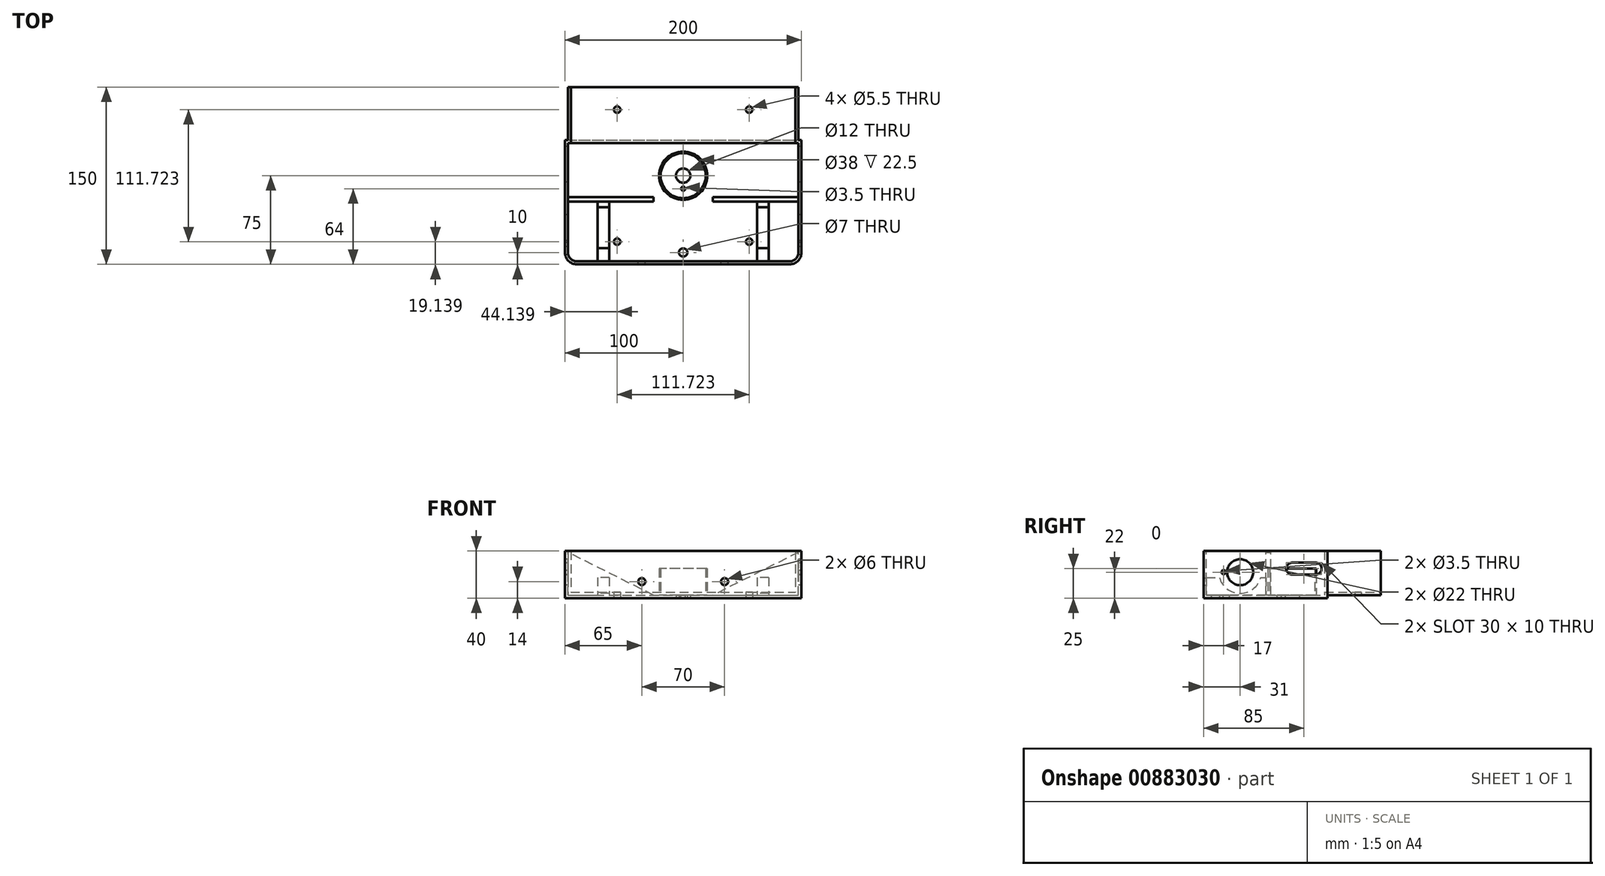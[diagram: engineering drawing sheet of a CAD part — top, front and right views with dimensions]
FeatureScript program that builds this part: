
annotation { "Feature Type Name" : "Feature", "Feature Type Description" : "" }
export const myFeature = defineFeature(function(context is Context, id is Id, definition is map)
    precondition{}
    {
        {
            var Q0;
            Q0=qCreatedBy(makeId("Top.planeOp"),FACE);
            var sketch = newSketch(context, id + "F0", { "sketchPlane" : qUnion([Q0])});
            skLineSegment(sketch, "E0.bottom", {"start": v(-100, -25) * mm, "end": v(100, -25) * mm});
            skLineSegment(sketch, "E0.top", {"start": v(-100, 125) * mm, "end": v(100, 125) * mm});
            skLineSegment(sketch, "E0.left", {"start": v(-100, -25) * mm, "end": v(-100, 125) * mm});
            skLineSegment(sketch, "E0.right", {"start": v(100, -25) * mm, "end": v(100, 125) * mm});
            skSolve(sketch);
        }
        {
            var Q0;
            Q0=makeQuery(id+"F0.imprint","IMPRINT",FACE,{"disambiguationData":[TD([[makeQuery(id+"F0.imprint","IMPRINT",EDGE,{"derivedFrom":sQuery(id+"F0.wireOp",EDGE,"E0.bottom")}),1.0]])]});
            extrude(context, id + "F1", {"entities" : qUnion([Q0]), "depth" : 40 * mm});
        }
        {
            var Q0;
            Q0=makeQuery(id+"F1.opExtrude","SWEPT_EDGE",EDGE,{"disambiguationData":[OSD([sQuery(id+"F0.wireOp",EDGE,"E0.bottom"),sQuery(id+"F0.wireOp",EDGE,"E0.left")])]});
            var Q1;
            Q1=makeQuery(id+"F1.opExtrude","SWEPT_EDGE",EDGE,{"disambiguationData":[OSD([sQuery(id+"F0.wireOp",EDGE,"E0.bottom"),sQuery(id+"F0.wireOp",EDGE,"E0.right")])]});
            fillet(context, id + "F2", {"entities" : qUnion([Q0, Q1]), "radius" : 10 * mm, "tangentPropagation" : true, "allowEdgeOverflow" : false});
        }
        {
            var Q0;
            Q0=qCreatedBy(makeId("Top.planeOp"),FACE);
            var sketch = newSketch(context, id + "F3", { "sketchPlane" : qUnion([Q0])});
            skLineSegment(sketch, "E1.bottom", {"start": v(-100, 180) * mm, "end": v(100, 180) * mm});
            skLineSegment(sketch, "E1.top", {"start": v(-100, 80) * mm, "end": v(100, 80) * mm});
            skLineSegment(sketch, "E1.left", {"start": v(-100, 180) * mm, "end": v(-100, 80) * mm});
            skLineSegment(sketch, "E1.right", {"start": v(100, 180) * mm, "end": v(100, 80) * mm});
            skSolve(sketch);
        }
        {
            var Q0;
            Q0=makeQuery(id+"F3.imprint","IMPRINT",FACE,{"disambiguationData":[TD([[makeQuery(id+"F3.imprint","IMPRINT",EDGE,{"derivedFrom":sQuery(id+"F3.wireOp",EDGE,"E1.bottom")}),-1.0]])]});
            extrude(context, id + "F4", {"entities" : qUnion([Q0]), "operationType" : NewBodyOperationType.REMOVE, "depth" : 2.5 * mm});
        }
        {
            var Q0;
            Q0=qCreatedBy(makeId("Top.planeOp"),FACE);
            var sketch = newSketch(context, id + "F5", { "sketchPlane" : qUnion([Q0])});
            skLineSegment(sketch, "E2.bottom", {"start": v(-137.5, 140) * mm, "end": v(-97.5, 140) * mm});
            skLineSegment(sketch, "E2.top", {"start": v(-137.5, 80) * mm, "end": v(-97.5, 80) * mm});
            skLineSegment(sketch, "E2.left", {"start": v(-137.5, 140) * mm, "end": v(-137.5, 80) * mm});
            skLineSegment(sketch, "E2.right", {"start": v(-97.5, 140) * mm, "end": v(-97.5, 80) * mm});
            skLineSegment(sketch, "E3.bottom", {"start": v(97.5, 140) * mm, "end": v(137.5, 140) * mm});
            skLineSegment(sketch, "E3.top", {"start": v(97.5, 80) * mm, "end": v(137.5, 80) * mm});
            skLineSegment(sketch, "E3.left", {"start": v(97.5, 140) * mm, "end": v(97.5, 80) * mm});
            skLineSegment(sketch, "E3.right", {"start": v(137.5, 140) * mm, "end": v(137.5, 80) * mm});
            skSolve(sketch);
        }
        {
            var Q0;
            Q0=qSketchRegion(id+"F5",true);
            extrude(context, id + "F6", {"entities" : qUnion([Q0]), "operationType" : NewBodyOperationType.REMOVE, "depth" : 200 * mm});
        }
        {
            var Q0;
            Q0=makeQuery(id+"F1.opExtrude","CAP_FACE",FACE,{"disambiguationData":[OSD([sQuery(id+"F0.wireOp",EDGE,"E0.bottom"),sQuery(id+"F0.wireOp",EDGE,"E0.top"),sQuery(id+"F0.wireOp",EDGE,"E0.left"),sQuery(id+"F0.wireOp",EDGE,"E0.right")])],"isStart":false});
            var Q1;
            Q1=makeQuery(id+"F1.opExtrude","SWEPT_FACE",FACE,{"disambiguationData":[OSD([sQuery(id+"F0.wireOp",EDGE,"E0.top")])]});
            shell(context, id + "F7", {"entities" : qUnion([Q0, Q1]), "thickness" : 2.5 * mm});
        }
        {
            var Q0;
            Q0=qCreatedBy(makeId("Right.planeOp"),FACE);
            var sketch = newSketch(context, id + "F8", { "sketchPlane" : qUnion([Q0])});
            skLineSegment(sketch, "E4.bottom", {"start": v(50, 30) * mm, "end": v(70, 30) * mm});
            skLineSegment(sketch, "E4.top", {"start": v(50, 20) * mm, "end": v(70, 20) * mm});
            skLineSegment(sketch, "E4.left", {"start": v(50, 30) * mm, "end": v(50, 20) * mm});
            skLineSegment(sketch, "E4.right", {"start": v(70, 30) * mm, "end": v(70, 20) * mm});
            skCircle(sketch, "E5", {"center": v(50, 25) * mm, "radius": 5 * mm});
            skCircle(sketch, "E6", {"center": v(70, 25) * mm, "radius": 5 * mm});
            skSolve(sketch);
        }
        {
            var Q0;
            {var subQ0=sQuery(id+"F8.wireOp",EDGE,"E4.left");Q0=makeQuery(id+"F8.imprint","IMPRINT",FACE,{"disambiguationData":[TD([[makeQuery(id+"F8.imprint","IMPRINT",EDGE,{"derivedFrom":subQ0}),-1.0]])]});}
            var Q1;
            {var subQ0=sQuery(id+"F8.wireOp",EDGE,"E4.left");Q1=makeQuery(id+"F8.imprint","IMPRINT",FACE,{"disambiguationData":[TD([[makeQuery(id+"F8.imprint","IMPRINT",EDGE,{"derivedFrom":subQ0}),1.0]])]});}
            var Q2;
            {var subQ0=sQuery(id+"F8.wireOp",EDGE,"E4.bottom");Q2=makeQuery(id+"F8.imprint","IMPRINT",FACE,{"disambiguationData":[TD([[makeQuery(id+"F8.imprint","IMPRINT",EDGE,{"derivedFrom":subQ0}),-1.0]])]});}
            var Q3;
            {var subQ0=sQuery(id+"F8.wireOp",EDGE,"E4.right");Q3=makeQuery(id+"F8.imprint","IMPRINT",FACE,{"disambiguationData":[TD([[makeQuery(id+"F8.imprint","IMPRINT",EDGE,{"derivedFrom":subQ0}),-1.0]])]});}
            var Q4;
            {var subQ0=sQuery(id+"F8.wireOp",EDGE,"E4.right");Q4=makeQuery(id+"F8.imprint","IMPRINT",FACE,{"disambiguationData":[TD([[makeQuery(id+"F8.imprint","IMPRINT",EDGE,{"derivedFrom":subQ0}),1.0]])]});}
            extrude(context, id + "F9", {"entities" : qUnion([Q0, Q1, Q2, Q3, Q4]), "operationType" : NewBodyOperationType.REMOVE, "endBound" : BoundingType.SYMMETRIC, "oppositeDirection" : true, "offsetDistance" : 25 * mm, "depth" : 300 * mm});
        }
        {
            var Q0;
            Q0=qCreatedBy(makeId("Top.planeOp"),FACE);
            var sketch = newSketch(context, id + "F10", { "sketchPlane" : qUnion([Q0])});
            skCircle(sketch, "E7", {"center": v(0, 50) * mm, "radius": 6 * mm});
            skSolve(sketch);
        }
        {
            var Q0;
            Q0=makeQuery(id+"F10.imprint","IMPRINT",FACE,{"disambiguationData":[TD([[makeQuery(id+"F10.imprint","IMPRINT",EDGE,{"derivedFrom":sQuery(id+"F10.wireOp",EDGE,"E7")}),1.0]])]});
            extrude(context, id + "F11", {"entities" : qUnion([Q0]), "operationType" : NewBodyOperationType.REMOVE, "depth" : 25 * mm});
        }
        {
            var Q0;
            Q0=qCreatedBy(makeId("Top.planeOp"),FACE);
            var sketch = newSketch(context, id + "F12", { "sketchPlane" : qUnion([Q0])});
            skCircle(sketch, "E8", {"center": v(0, 50) * mm, "radius": 20.4 * mm});
            skCircle(sketch, "E9", {"center": v(0, 50) * mm, "radius": 19 * mm});
            skSolve(sketch);
        }
        {
            var Q0;
            Q0=makeQuery(id+"F12.imprint","IMPRINT",FACE,{"disambiguationData":[TD([[makeQuery(id+"F12.imprint","IMPRINT",EDGE,{"derivedFrom":sQuery(id+"F12.wireOp",EDGE,"E8")}),1.0]])]});
            extrude(context, id + "F13", {"entities" : qUnion([Q0]), "operationType" : NewBodyOperationType.ADD, "depth" : 25 * mm});
        }
        {
            var Q0;
            Q0=qCreatedBy(makeId("Top.planeOp"),FACE);
            var sketch = newSketch(context, id + "F14", { "sketchPlane" : qUnion([Q0])});
            skCircle(sketch, "E10", {"center": v(-55.86, -5.86) * mm, "radius": 2.75 * mm});
            skCircle(sketch, "E11", {"center": v(55.86, -5.86) * mm, "radius": 2.75 * mm});
            skLineSegment(sketch, "E12", {"start": v(-55.86, -5.86) * mm, "end": v(0, 50) * mm, "construction": true});
            skLineSegment(sketch, "E13", {"start": v(0, 50) * mm, "end": v(55.86, -5.86) * mm, "construction": true});
            skLineSegment(sketch, "E14", {"start": v(0, 50) * mm, "end": v(55.86, 105.86) * mm, "construction": true});
            skLineSegment(sketch, "E15", {"start": v(0, 50) * mm, "end": v(-55.86, 105.86) * mm});
            skCircle(sketch, "E16", {"center": v(0, 50) * mm, "radius": 79 * mm, "construction": true});
            skCircle(sketch, "E17", {"center": v(55.86, 105.86) * mm, "radius": 2.75 * mm});
            skCircle(sketch, "E18", {"center": v(-55.86, 105.86) * mm, "radius": 2.75 * mm});
            skSolve(sketch);
        }
        {
            var Q0;
            Q0=qSketchRegion(id+"F14",true);
            extrude(context, id + "F15", {"entities" : qUnion([Q0]), "operationType" : NewBodyOperationType.REMOVE, "depth" : 25 * mm});
        }
        {
            var Q0;
            Q0=qCreatedBy(makeId("Front.planeOp"),FACE);
            var sketch = newSketch(context, id + "F16", { "sketchPlane" : qUnion([Q0])});
            skCircle(sketch, "E19", {"center": v(-35, 14) * mm, "radius": 3 * mm});
            skCircle(sketch, "E20", {"center": v(35, 14) * mm, "radius": 3 * mm});
            skSolve(sketch);
        }
        {
            var Q0;
            Q0=makeQuery(id+"F16.imprint","IMPRINT",FACE,{"disambiguationData":[TD([[makeQuery(id+"F16.imprint","IMPRINT",EDGE,{"derivedFrom":sQuery(id+"F16.wireOp",EDGE,"E19")}),1.0]])]});
            var Q1;
            Q1=makeQuery(id+"F16.imprint","IMPRINT",FACE,{"disambiguationData":[TD([[makeQuery(id+"F16.imprint","IMPRINT",EDGE,{"derivedFrom":sQuery(id+"F16.wireOp",EDGE,"E20")}),1.0]])]});
            extrude(context, id + "F17", {"entities" : qUnion([Q0, Q1]), "operationType" : NewBodyOperationType.REMOVE, "depth" : 200 * mm});
        }
        {
            var Q0;
            Q0=qCreatedBy(makeId("Top.planeOp"),FACE);
            var sketch = newSketch(context, id + "F18", { "sketchPlane" : qUnion([Q0])});
            skCircle(sketch, "E21", {"center": v(0, 50) * mm, "radius": 11 * mm, "construction": true});
            skCircle(sketch, "E22", {"center": v(0, 39) * mm, "radius": 1.75 * mm});
            skSolve(sketch);
        }
        {
            var Q0;
            Q0=qSketchRegion(id+"F18",true);
            extrude(context, id + "F19", {"entities" : qUnion([Q0]), "operationType" : NewBodyOperationType.REMOVE, "endBound" : BoundingType.SYMMETRIC, "oppositeDirection" : true, "depth" : 25 * mm});
        }
        {
            var Q0;
            Q0=qCreatedBy(makeId("Front.planeOp"),FACE);
            var sketch = newSketch(context, id + "F20", { "sketchPlane" : qUnion([Q0])});
            skLineSegment(sketch, "E23", {"start": v(-100, 0) * mm, "end": v(-20, 0) * mm});
            skLineSegment(sketch, "E24", {"start": v(-20, 0) * mm, "end": v(-100, 40) * mm});
            skLineSegment(sketch, "E25", {"start": v(-100, 40) * mm, "end": v(-100, 0) * mm});
            skLineSegment(sketch, "E26", {"start": v(20, 0) * mm, "end": v(100, 0) * mm});
            skLineSegment(sketch, "E27", {"start": v(100, 0) * mm, "end": v(100, 40) * mm});
            skLineSegment(sketch, "E28", {"start": v(100, 40) * mm, "end": v(20, 0) * mm});
            skSolve(sketch);
        }
        {
            var Q0;
            Q0=qSketchRegion(id+"F20",true);
            extrude(context, id + "F21", {"entities" : qUnion([Q0]), "operationType" : NewBodyOperationType.ADD, "oppositeDirection" : true, "depth" : 32 * mm, "hasSecondDirection" : true, "secondDirectionOppositeDirection" : true, "secondDirectionDepth" : 28 * mm});
        }
        {
            var Q0;
            Q0=qCreatedBy(makeId("Top.planeOp"),FACE);
            var sketch = newSketch(context, id + "F22", { "sketchPlane" : qUnion([Q0])});
            skCircle(sketch, "E29", {"center": v(0, -15) * mm, "radius": 3.5 * mm});
            skSolve(sketch);
        }
        {
            var Q0;
            Q0=qSketchRegion(id+"F22",true);
            extrude(context, id + "F23", {"entities" : qUnion([Q0]), "operationType" : NewBodyOperationType.REMOVE, "depth" : 25 * mm});
        }
        {
            var Q0;
            {var subQ0=sQuery(id+"F0.wireOp",EDGE,"E0.bottom");var subQ1=sQuery(id+"F0.wireOp",EDGE,"E0.right");var subQ2=sQuery(id+"F0.wireOp",EDGE,"E0.left");Q0=makeQuery(id+"F13.boolean.opBoolean","SPLIT",FACE,{"disambiguationData":[TD([makeQuery(id+"F7.opShell","OFFSET_FACE",FACE,{"disambiguationData":[OSD([subQ0])]})])],"derivedFrom":makeQuery(id+"F7.opShell","OFFSET_FACE",FACE,{"disambiguationData":[OSD([subQ0,sQuery(id+"F0.wireOp",EDGE,"E0.top"),subQ2,subQ1])]})});}
            var sketch = newSketch(context, id + "F24", { "sketchPlane" : qUnion([Q0])});
            skLineSegment(sketch, "E30.left", {"start": v(-72.5, -22.5) * mm, "end": v(-72.5, 28) * mm});
            skLineSegment(sketch, "E30.right", {"start": v(-62.5, -22.5) * mm, "end": v(-62.5, 28) * mm});
            skLineSegment(sketch, "E31.left", {"start": v(62.5, 28) * mm, "end": v(62.5, -22.5) * mm});
            skLineSegment(sketch, "E31.right", {"start": v(72.5, 28) * mm, "end": v(72.5, -22.5) * mm});
            skSolve(sketch);
        }
        {
            var Q0;
            {var subQ10=sQuery(id+"F24.wireOp",EDGE,"E30.left");Q0=makeQuery(id+"F24.imprint","IMPRINT",FACE,{"disambiguationData":[TD([[makeQuery(id+"F24.imprint","IMPRINT",EDGE,{"derivedFrom":subQ10}),-1.0]])]});}
            var Q1;
            {var subQ0=sQuery(id+"F24.wireOp",EDGE,"E31.left");Q1=makeQuery(id+"F24.imprint","IMPRINT",FACE,{"disambiguationData":[TD([[makeQuery(id+"F24.imprint","IMPRINT",EDGE,{"derivedFrom":subQ0}),1.0]])]});}
            extrude(context, id + "F25", {"entities" : qUnion([Q0, Q1]), "operationType" : NewBodyOperationType.ADD, "depth" : 15 * mm, "offsetDistance" : 25 * mm});
        }
        {
            var Q0;
            Q0=qCreatedBy(makeId("Right.planeOp"),FACE);
            var sketch = newSketch(context, id + "F26", { "sketchPlane" : qUnion([Q0])});
            skCircle(sketch, "E32", {"center": v(6, 22) * mm, "radius": 14 * mm, "construction": true});
            skCircle(sketch, "E33", {"center": v(-8, 22) * mm, "radius": 1.75 * mm});
            skLineSegment(sketch, "E34", {"start": v(6, 22) * mm, "end": v(-8, 22) * mm, "construction": true});
            skLineSegment(sketch, "E35", {"start": v(6, 22) * mm, "end": v(6, -15.46) * mm, "construction": true});
            skCircle(sketch, "E36", {"center": v(6, 22) * mm, "radius": 11 * mm});
            skCircle(sketch, "E37", {"center": v(6, 22) * mm, "radius": 18 * mm});
            skSolve(sketch);
        }
        {
            var Q0;
            Q0=makeQuery(id+"F26.imprint","IMPRINT",FACE,{"disambiguationData":[TD([[makeQuery(id+"F26.imprint","IMPRINT",EDGE,{"derivedFrom":sQuery(id+"F26.wireOp",EDGE,"E33")}),-1.0]])]});
            extrude(context, id + "F27", {"entities" : qUnion([Q0]), "operationType" : NewBodyOperationType.REMOVE, "endBound" : BoundingType.SYMMETRIC, "depth" : 190 * mm, "offsetDistance" : 25 * mm});
        }
        {
            var Q0;
            Q0=makeQuery(id+"F26.imprint","IMPRINT",FACE,{"disambiguationData":[TD([[makeQuery(id+"F26.imprint","IMPRINT",EDGE,{"derivedFrom":sQuery(id+"F26.wireOp",EDGE,"E33")}),1.0]])]});
            extrude(context, id + "F28", {"entities" : qUnion([Q0]), "operationType" : NewBodyOperationType.REMOVE, "oppositeDirection" : true, "offsetDistance" : 25 * mm, "depth" : 400 * mm, "hasSecondDirection" : true, "secondDirectionBound" : SecondDirectionBoundingType.THROUGH_ALL, "secondDirectionOppositeDirection" : false, "secondDirectionDepth" : 40 * mm});
        }
        {
            var Q0;
            Q0=makeQuery(id+"F26.imprint","IMPRINT",FACE,{"disambiguationData":[TD([[makeQuery(id+"F26.imprint","IMPRINT",EDGE,{"derivedFrom":sQuery(id+"F26.wireOp",EDGE,"E36")}),1.0]])]});
            var Q1;
            Q1=sQuery(id+"F26.wireOp",EDGE,"E36");
            extrude(context, id + "F29", {"entities" : qUnion([Q0]), "operationType" : NewBodyOperationType.REMOVE, "surfaceOperationType" : NewSurfaceOperationType.ADD, "surfaceEntities" : qUnion([Q1]), "endBound" : BoundingType.SYMMETRIC, "depth" : 390 * mm, "offsetDistance" : 25 * mm});
        }
    });
